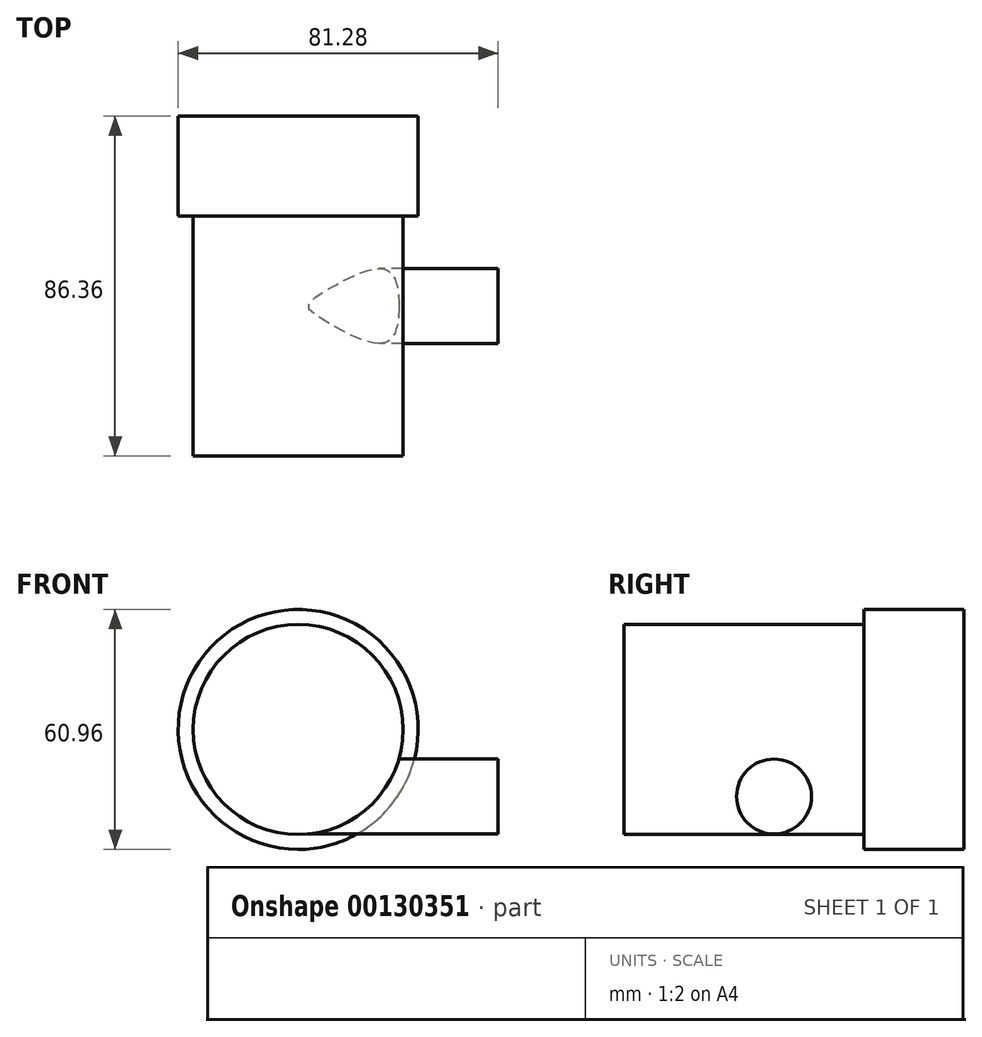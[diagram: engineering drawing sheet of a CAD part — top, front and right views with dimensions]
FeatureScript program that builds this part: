
annotation { "Feature Type Name" : "Feature", "Feature Type Description" : "" }
export const myFeature = defineFeature(function(context is Context, id is Id, definition is map)
    precondition{}
    {
        {
            var Q0;
            Q0=qCreatedBy(makeId("Front.planeOp"),FACE);
            var sketch = newSketch(context, id + "F0", { "sketchPlane" : qUnion([Q0])});
            skCircle(sketch, "E0", {"center": v(0, 0) * mm, "radius": 30.48 * mm});
            skSolve(sketch);
        }
        {
            var Q0;
            Q0=makeQuery(id+"F0.imprint","IMPRINT",FACE,{"disambiguationData":[TD([[makeQuery(id+"F0.imprint","IMPRINT",EDGE,{"derivedFrom":sQuery(id+"F0.wireOp",EDGE,"E0")}),1.0]])]});
            extrude(context, id + "F1", {"entities" : qUnion([Q0]), "depth" : 25.4 * mm});
        }
        {
            var Q0;
            Q0=makeQuery(id+"F1.opExtrude","CAP_FACE",FACE,{"disambiguationData":[OSD([sQuery(id+"F0.wireOp",EDGE,"E0")])],"isStart":false});
            var sketch = newSketch(context, id + "F2", { "sketchPlane" : qUnion([Q0])});
            skCircle(sketch, "E1", {"center": v(0, 0) * mm, "radius": 26.67 * mm});
            skSolve(sketch);
        }
        {
            var Q0;
            Q0=makeQuery(id+"F2.imprint","IMPRINT",FACE,{"disambiguationData":[TD([[makeQuery(id+"F2.imprint","IMPRINT",EDGE,{"derivedFrom":sQuery(id+"F2.wireOp",EDGE,"E1")}),1.0]])]});
            extrude(context, id + "F3", {"entities" : qUnion([Q0]), "operationType" : NewBodyOperationType.ADD, "depth" : 60.96 * mm});
        }
        {
            var Q0;
            Q0=qCreatedBy(makeId("Right.planeOp"),FACE);
            var sketch = newSketch(context, id + "F4", { "sketchPlane" : qUnion([Q0])});
            skCircle(sketch, "E2", {"center": v(-48.26, -17.04) * mm, "radius": 9.53 * mm});
            skSolve(sketch);
        }
        {
            var Q0;
            Q0 = qSketchRegion(id + "F4", true);
            extrude(context, id + "F5", {"entities" : qUnion([Q0]), "operationType" : NewBodyOperationType.ADD, "depth" : 50.8 * mm});
        }
    });
